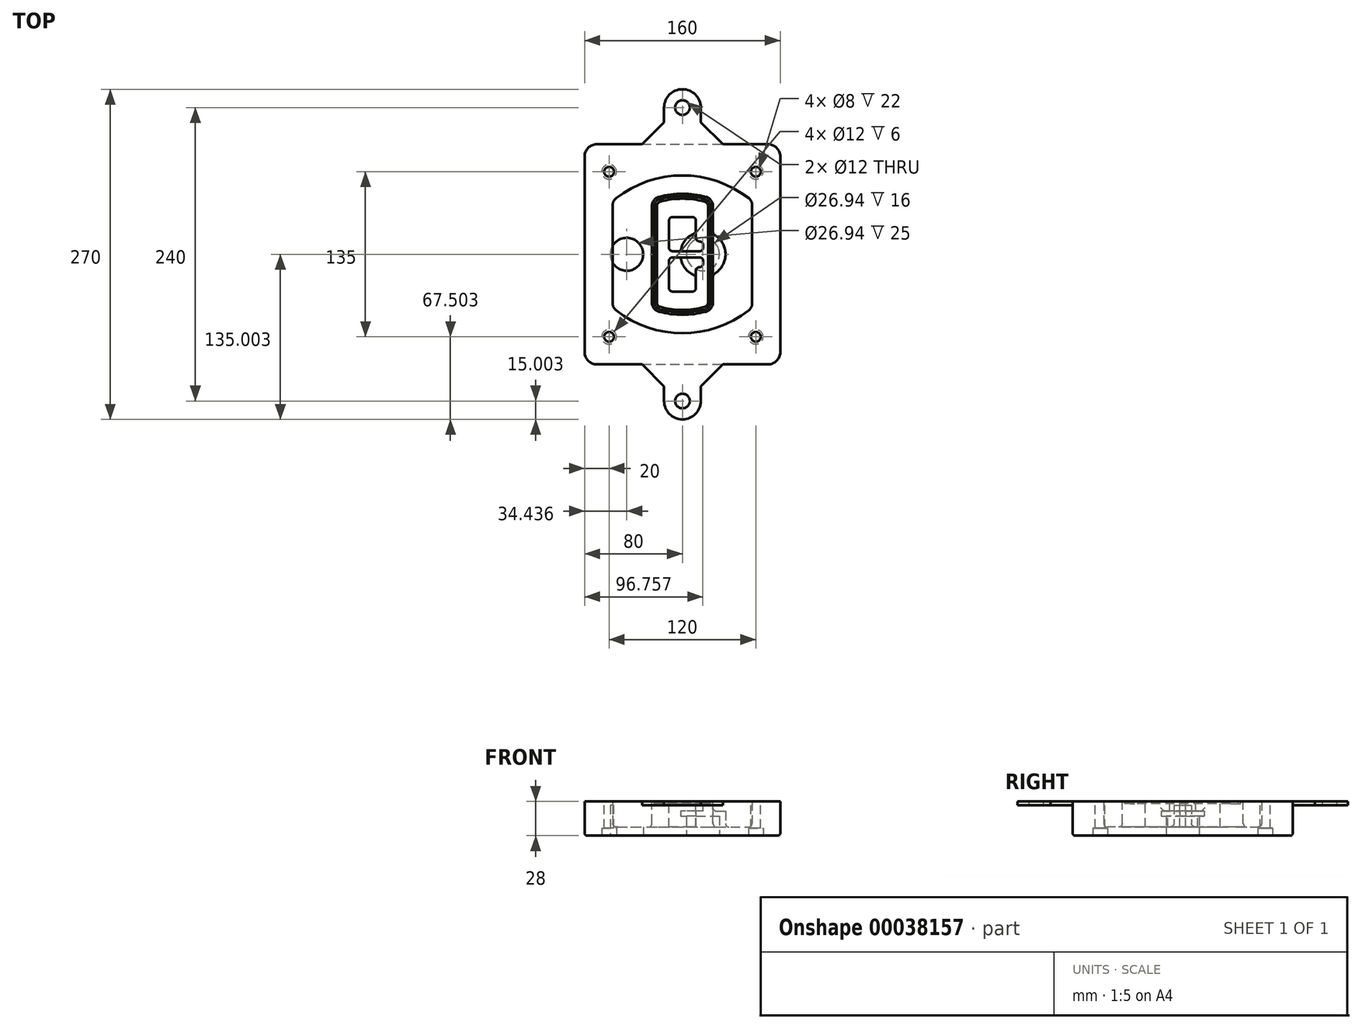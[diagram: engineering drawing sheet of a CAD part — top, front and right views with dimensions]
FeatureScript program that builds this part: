
annotation { "Feature Type Name" : "Feature", "Feature Type Description" : "" }
export const myFeature = defineFeature(function(context is Context, id is Id, definition is map)
    precondition{}
    {
        {
            var Q0;
            Q0=qCreatedBy(makeId("Top.planeOp"),FACE);
            var sketch = newSketch(context, id + "F0", { "sketchPlane" : qUnion([Q0])});
            skPoint(sketch, "E0.rect.middle", {"position": v(0, 0) * mm});
            skLineSegment(sketch, "E1.bottom", {"start": v(24.05, 28.38) * mm, "end": v(164.05, 28.38) * mm});
            skLineSegment(sketch, "E1.top", {"start": v(24.05, 208.38) * mm, "end": v(164.05, 208.38) * mm});
            skLineSegment(sketch, "E1.left", {"start": v(14.05, 38.38) * mm, "end": v(14.05, 198.38) * mm});
            skLineSegment(sketch, "E1.right", {"start": v(174.05, 38.38) * mm, "end": v(174.05, 198.38) * mm});
            skLineSegment(sketch, "E2", {"start": v(14.05, 208.38) * mm, "end": v(174.05, 28.38) * mm, "construction": true});
            skLineSegment(sketch, "E3", {"start": v(174.05, 208.38) * mm, "end": v(14.05, 28.38) * mm, "construction": true});
            skCircle(sketch, "E4", {"center": v(34.05, 185.88) * mm, "radius": 4 * mm});
            skCircle(sketch, "E5", {"center": v(154.05, 185.88) * mm, "radius": 4 * mm});
            skCircle(sketch, "E6", {"center": v(154.05, 50.88) * mm, "radius": 4 * mm});
            skCircle(sketch, "E7", {"center": v(34.05, 50.88) * mm, "radius": 4 * mm});
            skLineSegment(sketch, "E8", {"start": v(34.05, 185.88) * mm, "end": v(154.05, 185.88) * mm, "construction": true});
            skLineSegment(sketch, "E9", {"start": v(154.05, 185.88) * mm, "end": v(154.05, 50.88) * mm, "construction": true});
            skLineSegment(sketch, "E10", {"start": v(154.05, 50.88) * mm, "end": v(34.05, 50.88) * mm, "construction": true});
            skLineSegment(sketch, "E11", {"start": v(34.05, 50.88) * mm, "end": v(34.05, 185.88) * mm, "construction": true});
            skLineSegment(sketch, "E12", {"start": v(34.05, 158.68) * mm, "end": v(34.05, 78.09) * mm});
            skLineSegment(sketch, "E13", {"start": v(154.05, 158.68) * mm, "end": v(154.05, 78.09) * mm});
            skArc(sketch, "E14", {"start": v(150.2, 166.56) * mm, "mid": v(94.05, 185.88) * mm, "end": v(37.9, 166.56) * mm});
            skArc(sketch, "E15", {"start": v(37.9, 70.2) * mm, "mid": v(94.05, 50.88) * mm, "end": v(150.2, 70.2) * mm});
            skLineSegment(sketch, "E16", {"start": v(34.05, 118.38) * mm, "end": v(154.05, 118.38) * mm, "construction": true});
            skPoint(sketch, "E17.visualSharp", {"position": v(34.05, 73.38) * mm});
            skArc(sketch, "E17.filletArc", {"start": v(34.05, 78.09) * mm, "mid": v(35.06, 73.7) * mm, "end": v(37.9, 70.2) * mm});
            skPoint(sketch, "E18.visualSharp", {"position": v(34.05, 163.38) * mm});
            skArc(sketch, "E18.filletArc", {"start": v(37.9, 166.56) * mm, "mid": v(35.06, 163.06) * mm, "end": v(34.05, 158.68) * mm});
            skPoint(sketch, "E19.visualSharp", {"position": v(154.05, 163.38) * mm});
            skArc(sketch, "E19.filletArc", {"start": v(154.05, 158.68) * mm, "mid": v(153.04, 163.06) * mm, "end": v(150.2, 166.56) * mm});
            skPoint(sketch, "E20.visualSharp", {"position": v(154.05, 73.38) * mm});
            skArc(sketch, "E20.filletArc", {"start": v(150.2, 70.2) * mm, "mid": v(153.04, 73.7) * mm, "end": v(154.05, 78.09) * mm});
            skPoint(sketch, "E21.visualSharp", {"position": v(14.05, 208.38) * mm});
            skArc(sketch, "E21.filletArc", {"start": v(24.05, 208.38) * mm, "mid": v(16.98, 205.45) * mm, "end": v(14.05, 198.38) * mm});
            skPoint(sketch, "E22.visualSharp", {"position": v(174.05, 208.38) * mm});
            skArc(sketch, "E22.filletArc", {"start": v(174.05, 198.38) * mm, "mid": v(171.12, 205.45) * mm, "end": v(164.05, 208.38) * mm});
            skPoint(sketch, "E23.visualSharp", {"position": v(174.05, 28.38) * mm});
            skArc(sketch, "E23.filletArc", {"start": v(164.05, 28.38) * mm, "mid": v(171.12, 31.31) * mm, "end": v(174.05, 38.38) * mm});
            skPoint(sketch, "E24.visualSharp", {"position": v(14.05, 28.38) * mm});
            skArc(sketch, "E24.filletArc", {"start": v(14.05, 38.38) * mm, "mid": v(16.98, 31.31) * mm, "end": v(24.05, 28.38) * mm});
            skArc(sketch, "E25.0", {"start": v(151.05, 158.68) * mm, "mid": v(150.34, 161.75) * mm, "end": v(148.36, 164.2) * mm});
            skLineSegment(sketch, "E25.1", {"start": v(151.05, 158.68) * mm, "end": v(151.05, 78.09) * mm});
            skArc(sketch, "E25.2", {"start": v(148.36, 72.57) * mm, "mid": v(150.34, 75.02) * mm, "end": v(151.05, 78.09) * mm});
            skArc(sketch, "E25.3", {"start": v(39.74, 72.57) * mm, "mid": v(94.05, 53.88) * mm, "end": v(148.36, 72.57) * mm});
            skArc(sketch, "E25.4", {"start": v(37.05, 78.09) * mm, "mid": v(37.76, 75.02) * mm, "end": v(39.74, 72.57) * mm});
            skArc(sketch, "E25.5", {"start": v(148.36, 164.2) * mm, "mid": v(94.05, 182.88) * mm, "end": v(39.74, 164.2) * mm});
            skLineSegment(sketch, "E25.6", {"start": v(37.05, 158.68) * mm, "end": v(37.05, 78.09) * mm});
            skArc(sketch, "E25.7", {"start": v(39.74, 164.2) * mm, "mid": v(37.76, 161.75) * mm, "end": v(37.05, 158.68) * mm});
            skArc(sketch, "E26.0", {"start": v(35.43, 169.71) * mm, "mid": v(31.47, 164.82) * mm, "end": v(30.05, 158.68) * mm});
            skArc(sketch, "E26.1", {"start": v(152.67, 169.71) * mm, "mid": v(94.05, 189.88) * mm, "end": v(35.43, 169.71) * mm});
            skArc(sketch, "E26.2", {"start": v(158.05, 158.68) * mm, "mid": v(156.63, 164.82) * mm, "end": v(152.67, 169.71) * mm});
            skLineSegment(sketch, "E26.3", {"start": v(158.05, 158.68) * mm, "end": v(158.05, 78.09) * mm});
            skArc(sketch, "E26.4", {"start": v(152.67, 67.05) * mm, "mid": v(156.63, 71.95) * mm, "end": v(158.05, 78.09) * mm});
            skLineSegment(sketch, "E26.5", {"start": v(30.05, 158.68) * mm, "end": v(30.05, 78.09) * mm});
            skArc(sketch, "E26.6", {"start": v(35.43, 67.05) * mm, "mid": v(94.05, 46.88) * mm, "end": v(152.67, 67.05) * mm});
            skArc(sketch, "E26.7", {"start": v(30.05, 78.09) * mm, "mid": v(31.47, 71.95) * mm, "end": v(35.43, 67.05) * mm});
            skSolve(sketch);
        }
        {
            var Q0;
            Q0=makeQuery(id+"F0.imprint","IMPRINT",FACE,{"disambiguationData":[TD([[makeQuery(id+"F0.imprint","IMPRINT",EDGE,{"derivedFrom":sQuery(id+"F0.wireOp",EDGE,"E1.bottom")}),1.0]])]});
            var Q1;
            Q1=makeQuery(id+"F0.imprint","IMPRINT",FACE,{"disambiguationData":[TD([[makeQuery(id+"F0.imprint","IMPRINT",EDGE,{"derivedFrom":sQuery(id+"F0.wireOp",EDGE,"E12")}),1.0]])]});
            var Q2;
            Q2=makeQuery(id+"F0.imprint","IMPRINT",FACE,{"disambiguationData":[TD([[makeQuery(id+"F0.imprint","IMPRINT",EDGE,{"derivedFrom":sQuery(id+"F0.wireOp",EDGE,"E25.0")}),1.0]])]});
            var Q3;
            Q3=makeQuery(id+"F0.imprint","IMPRINT",FACE,{"disambiguationData":[TD([[makeQuery(id+"F0.imprint","IMPRINT",EDGE,{"derivedFrom":sQuery(id+"F0.wireOp",EDGE,"E12")}),-1.0]])]});
            extrude(context, id + "F1", {"entities" : qUnion([Q0, Q1, Q2, Q3]), "oppositeDirection" : true, "depth" : 25 * mm});
        }
        {
            var Q0;
            Q0=makeQuery(id+"F0.imprint","IMPRINT",FACE,{"disambiguationData":[TD([[makeQuery(id+"F0.imprint","IMPRINT",EDGE,{"derivedFrom":sQuery(id+"F0.wireOp",EDGE,"E12")}),1.0]])]});
            extrude(context, id + "F2", {"entities" : qUnion([Q0]), "operationType" : NewBodyOperationType.ADD, "depth" : 3 * mm});
        }
        {
            var Q0;
            Q0=makeQuery(id+"F0.imprint","IMPRINT",FACE,{"disambiguationData":[TD([[makeQuery(id+"F0.imprint","IMPRINT",EDGE,{"derivedFrom":sQuery(id+"F0.wireOp",EDGE,"E25.0")}),1.0]])]});
            extrude(context, id + "F3", {"entities" : qUnion([Q0]), "operationType" : NewBodyOperationType.REMOVE, "oppositeDirection" : true, "depth" : 18 * mm});
        }
        {
            var Q0;
            Q0=makeQuery(id+"F2.opExtrude","CAP_FACE",FACE,{"disambiguationData":[OSD([sQuery(id+"F0.wireOp",EDGE,"E12"),sQuery(id+"F0.wireOp",EDGE,"E13"),sQuery(id+"F0.wireOp",EDGE,"E14"),sQuery(id+"F0.wireOp",EDGE,"E15"),sQuery(id+"F0.wireOp",EDGE,"E17.filletArc"),sQuery(id+"F0.wireOp",EDGE,"E18.filletArc"),sQuery(id+"F0.wireOp",EDGE,"E19.filletArc"),sQuery(id+"F0.wireOp",EDGE,"E20.filletArc"),sQuery(id+"F0.wireOp",EDGE,"E25.0"),sQuery(id+"F0.wireOp",EDGE,"E25.1"),sQuery(id+"F0.wireOp",EDGE,"E25.2"),sQuery(id+"F0.wireOp",EDGE,"E25.3"),sQuery(id+"F0.wireOp",EDGE,"E25.4"),sQuery(id+"F0.wireOp",EDGE,"E25.5"),sQuery(id+"F0.wireOp",EDGE,"E25.6"),sQuery(id+"F0.wireOp",EDGE,"E25.7")])],"isStart":false});
            var sketch = newSketch(context, id + "F4", { "sketchPlane" : qUnion([Q0])});
            skArc(sketch, "E27.0", {"start": v(74.97, 71.41) * mm, "mid": v(94.05, 68.88) * mm, "end": v(113.13, 71.41) * mm});
            skArc(sketch, "E28.0", {"start": v(113.13, 165.35) * mm, "mid": v(94.05, 167.88) * mm, "end": v(74.97, 165.35) * mm});
            skLineSegment(sketch, "E29", {"start": v(69.05, 157.63) * mm, "end": v(69.05, 79.14) * mm});
            skLineSegment(sketch, "E30", {"start": v(119.05, 157.63) * mm, "end": v(119.05, 79.14) * mm});
            skLineSegment(sketch, "E31", {"start": v(69.05, 163.48) * mm, "end": v(119.05, 163.48) * mm, "construction": true});
            skLineSegment(sketch, "E32", {"start": v(69.05, 73.28) * mm, "end": v(119.05, 73.28) * mm, "construction": true});
            skPoint(sketch, "E33.visualSharp", {"position": v(69.05, 163.48) * mm});
            skArc(sketch, "E33.filletArc", {"start": v(74.97, 165.35) * mm, "mid": v(70.7, 162.5) * mm, "end": v(69.05, 157.63) * mm});
            skPoint(sketch, "E34.visualSharp", {"position": v(119.05, 163.48) * mm});
            skArc(sketch, "E34.filletArc", {"start": v(119.05, 157.63) * mm, "mid": v(117.4, 162.5) * mm, "end": v(113.13, 165.35) * mm});
            skPoint(sketch, "E35.visualSharp", {"position": v(119.05, 73.28) * mm});
            skArc(sketch, "E35.filletArc", {"start": v(113.13, 71.41) * mm, "mid": v(117.4, 74.27) * mm, "end": v(119.05, 79.14) * mm});
            skPoint(sketch, "E36.visualSharp", {"position": v(69.05, 73.28) * mm});
            skArc(sketch, "E36.filletArc", {"start": v(69.05, 79.14) * mm, "mid": v(70.7, 74.27) * mm, "end": v(74.97, 71.41) * mm});
            skArc(sketch, "E37.0", {"start": v(148.36, 164.2) * mm, "mid": v(94.05, 182.88) * mm, "end": v(39.74, 164.2) * mm});
            skArc(sketch, "E37.1", {"start": v(39.74, 164.2) * mm, "mid": v(37.76, 161.75) * mm, "end": v(37.05, 158.68) * mm});
            skLineSegment(sketch, "E37.2", {"start": v(37.05, 158.68) * mm, "end": v(37.05, 78.09) * mm});
            skArc(sketch, "E37.3", {"start": v(37.05, 78.09) * mm, "mid": v(37.76, 75.02) * mm, "end": v(39.74, 72.57) * mm});
            skArc(sketch, "E37.4", {"start": v(39.74, 72.57) * mm, "mid": v(94.05, 53.88) * mm, "end": v(148.36, 72.57) * mm});
            skArc(sketch, "E37.5", {"start": v(148.36, 72.57) * mm, "mid": v(150.34, 75.02) * mm, "end": v(151.05, 78.09) * mm});
            skLineSegment(sketch, "E37.6", {"start": v(151.05, 158.68) * mm, "end": v(151.05, 78.09) * mm});
            skArc(sketch, "E37.7", {"start": v(151.05, 158.68) * mm, "mid": v(150.34, 161.75) * mm, "end": v(148.36, 164.2) * mm});
            skLineSegment(sketch, "E38.0", {"start": v(117.05, 157.63) * mm, "end": v(117.05, 79.14) * mm});
            skArc(sketch, "E38.1", {"start": v(112.61, 73.34) * mm, "mid": v(115.81, 75.49) * mm, "end": v(117.05, 79.14) * mm});
            skArc(sketch, "E38.2", {"start": v(75.49, 73.34) * mm, "mid": v(94.05, 70.88) * mm, "end": v(112.61, 73.34) * mm});
            skArc(sketch, "E38.3", {"start": v(71.05, 79.14) * mm, "mid": v(72.29, 75.49) * mm, "end": v(75.49, 73.34) * mm});
            skLineSegment(sketch, "E38.4", {"start": v(71.05, 157.63) * mm, "end": v(71.05, 79.14) * mm});
            skArc(sketch, "E38.5", {"start": v(117.05, 157.63) * mm, "mid": v(115.81, 161.28) * mm, "end": v(112.61, 163.42) * mm});
            skArc(sketch, "E38.6", {"start": v(75.49, 163.42) * mm, "mid": v(72.29, 161.28) * mm, "end": v(71.05, 157.63) * mm});
            skArc(sketch, "E38.7", {"start": v(112.61, 163.42) * mm, "mid": v(94.05, 165.88) * mm, "end": v(75.49, 163.42) * mm});
            skArc(sketch, "E39.0", {"start": v(115.05, 157.63) * mm, "mid": v(114.23, 160.06) * mm, "end": v(112.1, 161.5) * mm});
            skLineSegment(sketch, "E39.1", {"start": v(115.05, 157.63) * mm, "end": v(115.05, 79.14) * mm});
            skArc(sketch, "E39.2", {"start": v(112.1, 75.27) * mm, "mid": v(114.23, 76.7) * mm, "end": v(115.05, 79.14) * mm});
            skArc(sketch, "E39.3", {"start": v(76, 75.27) * mm, "mid": v(94.05, 72.88) * mm, "end": v(112.1, 75.27) * mm});
            skArc(sketch, "E39.4", {"start": v(73.05, 79.14) * mm, "mid": v(73.87, 76.7) * mm, "end": v(76, 75.27) * mm});
            skArc(sketch, "E39.5", {"start": v(112.1, 161.5) * mm, "mid": v(94.05, 163.88) * mm, "end": v(76, 161.5) * mm});
            skLineSegment(sketch, "E39.6", {"start": v(73.05, 157.63) * mm, "end": v(73.05, 79.14) * mm});
            skArc(sketch, "E39.7", {"start": v(76, 161.5) * mm, "mid": v(73.87, 160.06) * mm, "end": v(73.05, 157.63) * mm});
            skLineSegment(sketch, "E40", {"start": v(69.05, 118.38) * mm, "end": v(119.05, 118.38) * mm, "construction": true});
            skLineSegment(sketch, "E41", {"start": v(83.05, 123.88) * mm, "end": v(83.05, 145.88) * mm});
            skLineSegment(sketch, "E42", {"start": v(86.05, 148.88) * mm, "end": v(102.05, 148.88) * mm});
            skLineSegment(sketch, "E43", {"start": v(105.05, 145.88) * mm, "end": v(105.05, 131.88) * mm});
            skLineSegment(sketch, "E44", {"start": v(108.05, 128.88) * mm, "end": v(108.05, 128.88) * mm});
            skLineSegment(sketch, "E45", {"start": v(111.05, 125.88) * mm, "end": v(111.05, 123.88) * mm});
            skLineSegment(sketch, "E46", {"start": v(108.05, 120.88) * mm, "end": v(86.05, 120.88) * mm});
            skPoint(sketch, "E47.visualSharp", {"position": v(83.05, 148.88) * mm});
            skArc(sketch, "E47.filletArc", {"start": v(86.05, 148.88) * mm, "mid": v(83.93, 148) * mm, "end": v(83.05, 145.88) * mm});
            skPoint(sketch, "E48.visualSharp", {"position": v(105.05, 148.88) * mm});
            skArc(sketch, "E48.filletArc", {"start": v(105.05, 145.88) * mm, "mid": v(104.17, 148) * mm, "end": v(102.05, 148.88) * mm});
            skPoint(sketch, "E49.visualSharp", {"position": v(105.05, 128.88) * mm});
            skArc(sketch, "E49.filletArc", {"start": v(105.05, 131.88) * mm, "mid": v(105.93, 129.76) * mm, "end": v(108.05, 128.88) * mm});
            skPoint(sketch, "E50.visualSharp", {"position": v(111.05, 128.88) * mm});
            skArc(sketch, "E50.filletArc", {"start": v(111.05, 125.88) * mm, "mid": v(110.17, 128) * mm, "end": v(108.05, 128.88) * mm});
            skPoint(sketch, "E51.visualSharp", {"position": v(111.05, 120.88) * mm});
            skArc(sketch, "E51.filletArc", {"start": v(108.05, 120.88) * mm, "mid": v(110.17, 121.76) * mm, "end": v(111.05, 123.88) * mm});
            skPoint(sketch, "E52.visualSharp", {"position": v(83.05, 120.88) * mm});
            skArc(sketch, "E52.filletArc", {"start": v(83.05, 123.88) * mm, "mid": v(83.93, 121.76) * mm, "end": v(86.05, 120.88) * mm});
            skLineSegment(sketch, "E53.0.MirrorCS", {"start": v(108.05, 115.88) * mm, "end": v(86.05, 115.88) * mm});
            skArc(sketch, "E54.0.MirrorCS", {"start": v(83.05, 112.88) * mm, "mid": v(83.93, 115) * mm, "end": v(86.05, 115.88) * mm});
            skLineSegment(sketch, "E55.0.MirrorCS", {"start": v(83.05, 112.88) * mm, "end": v(83.05, 90.88) * mm});
            skArc(sketch, "E56.0.MirrorCS", {"start": v(86.05, 87.88) * mm, "mid": v(83.93, 88.76) * mm, "end": v(83.05, 90.88) * mm});
            skLineSegment(sketch, "E57.0.MirrorCS", {"start": v(86.05, 87.88) * mm, "end": v(102.05, 87.88) * mm});
            skArc(sketch, "E58.0.MirrorCS", {"start": v(105.05, 90.88) * mm, "mid": v(104.17, 88.76) * mm, "end": v(102.05, 87.88) * mm});
            skLineSegment(sketch, "E59.0.MirrorCS", {"start": v(105.05, 90.88) * mm, "end": v(105.05, 104.88) * mm});
            skArc(sketch, "E60.0.MirrorCS", {"start": v(105.05, 104.88) * mm, "mid": v(105.93, 107) * mm, "end": v(108.05, 107.88) * mm});
            skArc(sketch, "E61.0.MirrorCS", {"start": v(111.05, 110.88) * mm, "mid": v(110.17, 108.76) * mm, "end": v(108.05, 107.88) * mm});
            skLineSegment(sketch, "E62.0.MirrorCS", {"start": v(111.05, 110.88) * mm, "end": v(111.05, 112.88) * mm});
            skArc(sketch, "E63.0.MirrorCS", {"start": v(108.05, 115.88) * mm, "mid": v(110.17, 115) * mm, "end": v(111.05, 112.88) * mm});
            skSolve(sketch);
        }
        {
            var Q0;
            Q0=makeQuery(id+"F4.imprint","IMPRINT",FACE,{"disambiguationData":[TD([[makeQuery(id+"F4.imprint","IMPRINT",EDGE,{"derivedFrom":sQuery(id+"F4.wireOp",EDGE,"E27.0")}),1.0]])]});
            var Q1;
            Q1=makeQuery(id+"F4.imprint","IMPRINT",FACE,{"disambiguationData":[TD([[makeQuery(id+"F4.imprint","IMPRINT",EDGE,{"derivedFrom":sQuery(id+"F4.wireOp",EDGE,"E38.0")}),-1.0]])]});
            var Q2;
            Q2=makeQuery(id+"F4.imprint","IMPRINT",FACE,{"disambiguationData":[TD([[makeQuery(id+"F4.imprint","IMPRINT",EDGE,{"derivedFrom":sQuery(id+"F4.wireOp",EDGE,"E39.0")}),1.0]])]});
            extrude(context, id + "F5", {"entities" : qUnion([Q0, Q1, Q2]), "operationType" : NewBodyOperationType.ADD, "endBound" : BoundingType.UP_TO_NEXT, "oppositeDirection" : true, "depth" : 25 * mm});
        }
        {
            var Q0;
            Q0=makeQuery(id+"F4.imprint","IMPRINT",FACE,{"disambiguationData":[TD([[makeQuery(id+"F4.imprint","IMPRINT",EDGE,{"derivedFrom":sQuery(id+"F4.wireOp",EDGE,"E38.0")}),-1.0]])]});
            extrude(context, id + "F6", {"entities" : qUnion([Q0]), "operationType" : NewBodyOperationType.REMOVE, "oppositeDirection" : true, "depth" : 2 * mm});
        }
        {
            var Q0;
            Q0=makeQuery(id+"F1.opExtrude","CAP_FACE",FACE,{"disambiguationData":[OSD([sQuery(id+"F0.wireOp",EDGE,"E1.bottom"),sQuery(id+"F0.wireOp",EDGE,"E1.top"),sQuery(id+"F0.wireOp",EDGE,"E1.left"),sQuery(id+"F0.wireOp",EDGE,"E1.right"),sQuery(id+"F0.wireOp",EDGE,"E4"),sQuery(id+"F0.wireOp",EDGE,"E5"),sQuery(id+"F0.wireOp",EDGE,"E6"),sQuery(id+"F0.wireOp",EDGE,"E7"),sQuery(id+"F0.wireOp",EDGE,"E21.filletArc"),sQuery(id+"F0.wireOp",EDGE,"E22.filletArc"),sQuery(id+"F0.wireOp",EDGE,"E23.filletArc"),sQuery(id+"F0.wireOp",EDGE,"E24.filletArc")])],"isStart":false});
            var sketch = newSketch(context, id + "F7", { "sketchPlane" : qUnion([Q0])});
            skCircle(sketch, "E64", {"center": v(110.8, -118.38) * mm, "radius": 13.47 * mm});
            skCircle(sketch, "E65", {"center": v(48.49, -118.38) * mm, "radius": 13.47 * mm});
            skLineSegment(sketch, "E66", {"start": v(174.05, -118.38) * mm, "end": v(14.05, -118.38) * mm});
            skCircle(sketch, "E67", {"center": v(110.8, -118.38) * mm, "radius": 18.47 * mm});
            skCircle(sketch, "E68", {"center": v(154.05, -185.88) * mm, "radius": 6 * mm});
            skCircle(sketch, "E69", {"center": v(34.05, -185.88) * mm, "radius": 6 * mm});
            skCircle(sketch, "E70", {"center": v(34.05, -50.88) * mm, "radius": 6 * mm});
            skCircle(sketch, "E71", {"center": v(154.05, -50.88) * mm, "radius": 6 * mm});
            skSolve(sketch);
        }
        {
            var Q0;
            {var subQ1=sQuery(id+"F7.wireOp",EDGE,"E66");var subQ4=sQuery(id+"F7.wireOp",EDGE,"E64");var subQ6=makeQuery(id+"F7.imprint","INTERSECT",VERTEX,{"disambiguationData":[OD(0.0)],"derivedFrom":[subQ4,subQ1]});Q0=makeQuery(id+"F7.imprint","IMPRINT",FACE,{"disambiguationData":[TD([[makeQuery(id+"F7.imprint","IMPRINT",EDGE,{"disambiguationData":[TD([[subQ6,-1.0]])],"derivedFrom":subQ4}),-1.0]])]});}
            var Q1;
            {var subQ0=sQuery(id+"F7.wireOp",EDGE,"E66");var subQ1=sQuery(id+"F7.wireOp",EDGE,"E64");var subQ3=makeQuery(id+"F7.imprint","INTERSECT",VERTEX,{"disambiguationData":[OD(0.0)],"derivedFrom":[subQ1,subQ0]});Q1=makeQuery(id+"F7.imprint","IMPRINT",FACE,{"disambiguationData":[TD([[makeQuery(id+"F7.imprint","IMPRINT",EDGE,{"disambiguationData":[TD([[subQ3,-1.0]])],"derivedFrom":subQ1}),1.0]])]});}
            var Q2;
            {var subQ0=sQuery(id+"F7.wireOp",EDGE,"E66");var subQ1=sQuery(id+"F7.wireOp",EDGE,"E64");var subQ3=makeQuery(id+"F7.imprint","INTERSECT",VERTEX,{"disambiguationData":[OD(0.0)],"derivedFrom":[subQ1,subQ0]});Q2=makeQuery(id+"F7.imprint","IMPRINT",FACE,{"disambiguationData":[TD([[makeQuery(id+"F7.imprint","IMPRINT",EDGE,{"disambiguationData":[TD([[subQ3,1.0]])],"derivedFrom":subQ1}),1.0]])]});}
            var Q3;
            {var subQ1=sQuery(id+"F7.wireOp",EDGE,"E66");var subQ4=sQuery(id+"F7.wireOp",EDGE,"E64");var subQ6=makeQuery(id+"F7.imprint","INTERSECT",VERTEX,{"disambiguationData":[OD(0.0)],"derivedFrom":[subQ4,subQ1]});Q3=makeQuery(id+"F7.imprint","IMPRINT",FACE,{"disambiguationData":[TD([[makeQuery(id+"F7.imprint","IMPRINT",EDGE,{"disambiguationData":[TD([[subQ6,1.0]])],"derivedFrom":subQ4}),-1.0]])]});}
            extrude(context, id + "F8", {"entities" : qUnion([Q0, Q1, Q2, Q3]), "operationType" : NewBodyOperationType.ADD, "oppositeDirection" : true, "depth" : 20 * mm});
        }
        {
            var Q0;
            {var subQ0=sQuery(id+"F7.wireOp",EDGE,"E66");var subQ1=sQuery(id+"F7.wireOp",EDGE,"E64");var subQ3=makeQuery(id+"F7.imprint","INTERSECT",VERTEX,{"disambiguationData":[OD(0.0)],"derivedFrom":[subQ1,subQ0]});Q0=makeQuery(id+"F7.imprint","IMPRINT",FACE,{"disambiguationData":[TD([[makeQuery(id+"F7.imprint","IMPRINT",EDGE,{"disambiguationData":[TD([[subQ3,-1.0]])],"derivedFrom":subQ1}),1.0]])]});}
            var Q1;
            {var subQ0=sQuery(id+"F7.wireOp",EDGE,"E66");var subQ1=sQuery(id+"F7.wireOp",EDGE,"E64");var subQ3=makeQuery(id+"F7.imprint","INTERSECT",VERTEX,{"disambiguationData":[OD(0.0)],"derivedFrom":[subQ1,subQ0]});Q1=makeQuery(id+"F7.imprint","IMPRINT",FACE,{"disambiguationData":[TD([[makeQuery(id+"F7.imprint","IMPRINT",EDGE,{"disambiguationData":[TD([[subQ3,1.0]])],"derivedFrom":subQ1}),1.0]])]});}
            extrude(context, id + "F9", {"entities" : qUnion([Q0, Q1]), "operationType" : NewBodyOperationType.REMOVE, "oppositeDirection" : true, "depth" : 16 * mm});
        }
        {
            var Q0;
            {var subQ0=sQuery(id+"F7.wireOp",EDGE,"E66");var subQ1=sQuery(id+"F7.wireOp",EDGE,"E65");var subQ3=makeQuery(id+"F7.imprint","INTERSECT",VERTEX,{"disambiguationData":[OD(0.0)],"derivedFrom":[subQ1,subQ0]});Q0=makeQuery(id+"F7.imprint","IMPRINT",FACE,{"disambiguationData":[TD([[makeQuery(id+"F7.imprint","IMPRINT",EDGE,{"disambiguationData":[TD([[subQ3,-1.0]])],"derivedFrom":subQ1}),1.0]])]});}
            var Q1;
            {var subQ0=sQuery(id+"F7.wireOp",EDGE,"E66");var subQ1=sQuery(id+"F7.wireOp",EDGE,"E65");var subQ3=makeQuery(id+"F7.imprint","INTERSECT",VERTEX,{"disambiguationData":[OD(0.0)],"derivedFrom":[subQ1,subQ0]});Q1=makeQuery(id+"F7.imprint","IMPRINT",FACE,{"disambiguationData":[TD([[makeQuery(id+"F7.imprint","IMPRINT",EDGE,{"disambiguationData":[TD([[subQ3,1.0]])],"derivedFrom":subQ1}),1.0]])]});}
            extrude(context, id + "F10", {"entities" : qUnion([Q0, Q1]), "operationType" : NewBodyOperationType.REMOVE, "oppositeDirection" : true, "depth" : 25 * mm});
        }
        {
            var Q0;
            Q0=makeQuery(id+"F7.imprint","IMPRINT",FACE,{"disambiguationData":[TD([[makeQuery(id+"F7.imprint","IMPRINT",EDGE,{"derivedFrom":sQuery(id+"F7.wireOp",EDGE,"E68")}),1.0]])]});
            var Q1;
            Q1=makeQuery(id+"F7.imprint","IMPRINT",FACE,{"disambiguationData":[TD([[makeQuery(id+"F7.imprint","IMPRINT",EDGE,{"derivedFrom":makeQuery(id+"F1.opExtrude","CAP_EDGE",EDGE,{"disambiguationData":[OSD([sQuery(id+"F0.wireOp",EDGE,"E5")])],"isStart":false})}),-1.0]])]});
            var Q2;
            Q2=makeQuery(id+"F7.imprint","IMPRINT",FACE,{"disambiguationData":[TD([[makeQuery(id+"F7.imprint","IMPRINT",EDGE,{"derivedFrom":sQuery(id+"F7.wireOp",EDGE,"E69")}),1.0]])]});
            var Q3;
            Q3=makeQuery(id+"F7.imprint","IMPRINT",FACE,{"disambiguationData":[TD([[makeQuery(id+"F7.imprint","IMPRINT",EDGE,{"derivedFrom":makeQuery(id+"F1.opExtrude","CAP_EDGE",EDGE,{"disambiguationData":[OSD([sQuery(id+"F0.wireOp",EDGE,"E4")])],"isStart":false})}),-1.0]])]});
            var Q4;
            Q4=makeQuery(id+"F7.imprint","IMPRINT",FACE,{"disambiguationData":[TD([[makeQuery(id+"F7.imprint","IMPRINT",EDGE,{"derivedFrom":sQuery(id+"F7.wireOp",EDGE,"E70")}),1.0]])]});
            var Q5;
            Q5=makeQuery(id+"F7.imprint","IMPRINT",FACE,{"disambiguationData":[TD([[makeQuery(id+"F7.imprint","IMPRINT",EDGE,{"derivedFrom":makeQuery(id+"F1.opExtrude","CAP_EDGE",EDGE,{"disambiguationData":[OSD([sQuery(id+"F0.wireOp",EDGE,"E7")])],"isStart":false})}),-1.0]])]});
            var Q6;
            Q6=makeQuery(id+"F7.imprint","IMPRINT",FACE,{"disambiguationData":[TD([[makeQuery(id+"F7.imprint","IMPRINT",EDGE,{"derivedFrom":sQuery(id+"F7.wireOp",EDGE,"E71")}),1.0]])]});
            var Q7;
            Q7=makeQuery(id+"F7.imprint","IMPRINT",FACE,{"disambiguationData":[TD([[makeQuery(id+"F7.imprint","IMPRINT",EDGE,{"derivedFrom":makeQuery(id+"F1.opExtrude","CAP_EDGE",EDGE,{"disambiguationData":[OSD([sQuery(id+"F0.wireOp",EDGE,"E6")])],"isStart":false})}),-1.0]])]});
            extrude(context, id + "F11", {"entities" : qUnion([Q0, Q1, Q2, Q3, Q4, Q5, Q6, Q7]), "operationType" : NewBodyOperationType.REMOVE, "oppositeDirection" : true, "depth" : 6 * mm});
        }
        {
            var Q0;
            Q0=makeQuery(id+"F9.boolean.opBoolean","COPY",FACE,{"derivedFrom":makeQuery(id+"F9.opExtrude","CAP_FACE",FACE,{"disambiguationData":[OSD([sQuery(id+"F7.wireOp",EDGE,"E64")])],"isStart":false})});
            var sketch = newSketch(context, id + "F12", { "sketchPlane" : qUnion([Q0])});
            skArc(sketch, "E72.0", {"start": v(105.05, -100.83) * mm, "mid": v(96.62, -106.56) * mm, "end": v(92.5, -115.88) * mm});
            skArc(sketch, "E72.1", {"start": v(92.5, -120.88) * mm, "mid": v(96.62, -130.2) * mm, "end": v(105.05, -135.93) * mm});
            skLineSegment(sketch, "E73", {"start": v(92.5, -120.88) * mm, "end": v(108.05, -120.88) * mm});
            skLineSegment(sketch, "E74.0", {"start": v(108.05, -115.88) * mm, "end": v(92.5, -115.88) * mm});
            skArc(sketch, "E74.1", {"start": v(108.05, -115.88) * mm, "mid": v(110.17, -115) * mm, "end": v(111.05, -112.88) * mm});
            skLineSegment(sketch, "E74.2", {"start": v(111.05, -110.88) * mm, "end": v(111.05, -112.88) * mm});
            skArc(sketch, "E74.3", {"start": v(111.05, -110.88) * mm, "mid": v(110.17, -108.76) * mm, "end": v(108.05, -107.88) * mm});
            skArc(sketch, "E74.4", {"start": v(105.05, -104.88) * mm, "mid": v(105.93, -107) * mm, "end": v(108.05, -107.88) * mm});
            skLineSegment(sketch, "E74.5", {"start": v(105.05, -100.83) * mm, "end": v(105.05, -104.88) * mm});
            skLineSegment(sketch, "E74.7", {"start": v(108.05, -120.88) * mm, "end": v(92.5, -120.88) * mm});
            skArc(sketch, "E74.8", {"start": v(108.05, -120.88) * mm, "mid": v(110.17, -121.76) * mm, "end": v(111.05, -123.88) * mm});
            skLineSegment(sketch, "E74.9", {"start": v(111.05, -125.88) * mm, "end": v(111.05, -123.88) * mm});
            skArc(sketch, "E74.10", {"start": v(111.05, -125.88) * mm, "mid": v(110.17, -128) * mm, "end": v(108.05, -128.88) * mm});
            skArc(sketch, "E74.11", {"start": v(105.05, -131.88) * mm, "mid": v(105.93, -129.76) * mm, "end": v(108.05, -128.88) * mm});
            skLineSegment(sketch, "E74.12", {"start": v(105.05, -135.93) * mm, "end": v(105.05, -131.88) * mm});
            skPoint(sketch, "E75.orphan", {"position": v(105.05, -145.88) * mm});
            skPoint(sketch, "E76.orphan", {"position": v(86.05, -120.88) * mm});
            skPoint(sketch, "E77.orphan", {"position": v(86.05, -115.88) * mm});
            skPoint(sketch, "E78.orphan", {"position": v(105.05, -90.88) * mm});
            skSolve(sketch);
        }
        {
            var Q0;
            {var subQ7=sQuery(id+"F12.wireOp",EDGE,"E72.0");var subQ14=sQuery(id+"F12.wireOp",EDGE,"E72.1");var subQ16=sQuery(id+"F12.wireOp",EDGE,"E74.1");var subQ18=sQuery(id+"F12.wireOp",EDGE,"E74.8");Q0=qUnion([makeQuery(id+"F12.imprint","IMPRINT",FACE,{"disambiguationData":[TD([[makeQuery(id+"F12.imprint","IMPRINT",EDGE,{"derivedFrom":subQ7}),1.0]])]}),makeQuery(id+"F12.imprint","IMPRINT",FACE,{"disambiguationData":[TD([[makeQuery(id+"F12.imprint","IMPRINT",EDGE,{"derivedFrom":subQ14}),1.0]])]}),makeQuery(id+"F12.imprint","IMPRINT",FACE,{"disambiguationData":[TD([[makeQuery(id+"F12.imprint","IMPRINT",EDGE,{"derivedFrom":subQ16}),1.0]])]}),makeQuery(id+"F12.imprint","IMPRINT",FACE,{"disambiguationData":[TD([[makeQuery(id+"F12.imprint","IMPRINT",EDGE,{"derivedFrom":subQ18}),-1.0]])]})]);}
            var Q1;
            Q1=makeQuery(id+"F5.boolean.opBoolean","SPLIT",FACE,{"disambiguationData":[TD([makeQuery(id+"F5.opExtrude","SWEPT_FACE",FACE,{"disambiguationData":[OSD([sQuery(id+"F4.wireOp",EDGE,"E41")])]})])],"derivedFrom":makeQuery(id+"F3.boolean.opBoolean","COPY",FACE,{"derivedFrom":makeQuery(id+"F3.opExtrude","CAP_FACE",FACE,{"disambiguationData":[OSD([sQuery(id+"F0.wireOp",EDGE,"E25.0"),sQuery(id+"F0.wireOp",EDGE,"E25.1"),sQuery(id+"F0.wireOp",EDGE,"E25.2"),sQuery(id+"F0.wireOp",EDGE,"E25.3"),sQuery(id+"F0.wireOp",EDGE,"E25.4"),sQuery(id+"F0.wireOp",EDGE,"E25.5"),sQuery(id+"F0.wireOp",EDGE,"E25.6"),sQuery(id+"F0.wireOp",EDGE,"E25.7")])],"isStart":false})})});
            extrude(context, id + "F13", {"entities" : qUnion([Q0]), "operationType" : NewBodyOperationType.REMOVE, "endBound" : BoundingType.UP_TO_SURFACE, "endBoundEntityFace" : qUnion([Q1]), "depth" : 25 * mm});
        }
        {
            var Q0;
            Q0=makeQuery(id+"F3.boolean.opBoolean","COPY",EDGE,{"derivedFrom":makeQuery(id+"F3.opExtrude","CAP_EDGE",EDGE,{"disambiguationData":[OSD([sQuery(id+"F0.wireOp",EDGE,"E25.6")])],"isStart":false})});
            var Q1;
            Q1=makeQuery(id+"F8.boolean.opBoolean","INTERSECT",EDGE,{"derivedFrom":[makeQuery(id+"F5.opExtrude","SWEPT_FACE",FACE,{"disambiguationData":[OSD([sQuery(id+"F4.wireOp",EDGE,"E30")])]}),makeQuery(id+"F8.opExtrude","CAP_FACE",FACE,{"disambiguationData":[OSD([sQuery(id+"F7.wireOp",EDGE,"E67")])],"isStart":false})]});
            var Q2;
            Q2=makeQuery(id+"F8.boolean.opBoolean","INTERSECT",EDGE,{"disambiguationData":[OD(1.0)],"derivedFrom":[makeQuery(id+"F5.opExtrude","SWEPT_FACE",FACE,{"disambiguationData":[OSD([sQuery(id+"F4.wireOp",EDGE,"E30")])]}),makeQuery(id+"F8.opExtrude","SWEPT_FACE",FACE,{"disambiguationData":[OSD([sQuery(id+"F7.wireOp",EDGE,"E67")])]})]});
            var Q3;
            {var subQ0=sQuery(id+"F4.wireOp",EDGE,"E30");Q3=makeQuery(id+"F8.boolean.opBoolean","SPLIT",EDGE,{"disambiguationData":[TD([makeQuery(id+"F5.opExtrude","SWEPT_FACE",FACE,{"disambiguationData":[OSD([sQuery(id+"F4.wireOp",EDGE,"E35.filletArc")])]})])],"derivedFrom":makeQuery(id+"F5.opExtrude","CAP_EDGE",EDGE,{"disambiguationData":[OSD([subQ0])],"isStart":false})});}
            var Q4;
            {var subQ0=sQuery(id+"F0.wireOp",EDGE,"E25.7");var subQ1=sQuery(id+"F0.wireOp",EDGE,"E25.1");var subQ2=sQuery(id+"F0.wireOp",EDGE,"E25.6");var subQ3=sQuery(id+"F0.wireOp",EDGE,"E25.5");var subQ4=sQuery(id+"F0.wireOp",EDGE,"E25.4");var subQ5=sQuery(id+"F0.wireOp",EDGE,"E25.0");var subQ6=sQuery(id+"F0.wireOp",EDGE,"E25.2");var subQ7=sQuery(id+"F0.wireOp",EDGE,"E25.3");Q4=makeQuery(id+"F8.boolean.opBoolean","INTERSECT",EDGE,{"derivedFrom":[makeQuery(id+"F5.boolean.opBoolean","SPLIT",FACE,{"disambiguationData":[TD([makeQuery(id+"F2.opExtrude","SWEPT_FACE",FACE,{"disambiguationData":[OSD([subQ5])]})])],"derivedFrom":makeQuery(id+"F3.boolean.opBoolean","COPY",FACE,{"derivedFrom":makeQuery(id+"F3.opExtrude","CAP_FACE",FACE,{"disambiguationData":[OSD([subQ5,subQ1,subQ6,subQ7,subQ4,subQ3,subQ2,subQ0])],"isStart":false})})}),makeQuery(id+"F8.opExtrude","SWEPT_FACE",FACE,{"disambiguationData":[OSD([sQuery(id+"F7.wireOp",EDGE,"E67")])]})]});}
            var Q5;
            Q5=makeQuery(id+"F8.boolean.opBoolean","INTERSECT",EDGE,{"disambiguationData":[OD(0.0)],"derivedFrom":[makeQuery(id+"F5.opExtrude","SWEPT_FACE",FACE,{"disambiguationData":[OSD([sQuery(id+"F4.wireOp",EDGE,"E30")])]}),makeQuery(id+"F8.opExtrude","SWEPT_FACE",FACE,{"disambiguationData":[OSD([sQuery(id+"F7.wireOp",EDGE,"E67")])]})]});
            fillet(context, id + "F14", {"entities" : qUnion([Q0, Q1, Q2, Q3, Q4, Q5]), "radius" : 3 * mm, "tangentPropagation" : true, "allowEdgeOverflow" : false});
        }
        {
            var Q0;
            Q0=makeQuery(id+"F1.opExtrude","CAP_EDGE",EDGE,{"disambiguationData":[OSD([sQuery(id+"F0.wireOp",EDGE,"E1.bottom")])],"isStart":false});
            fillet(context, id + "F15", {"entities" : qUnion([Q0]), "radius" : 2 * mm, "tangentPropagation" : true, "allowEdgeOverflow" : false});
        }
        {
            var Q0;
            {var subQ0=sQuery(id+"F0.wireOp",EDGE,"E1.bottom");var subQ1=sQuery(id+"F0.wireOp",EDGE,"E1.top");var subQ2=sQuery(id+"F0.wireOp",EDGE,"E1.left");var subQ3=sQuery(id+"F0.wireOp",EDGE,"E1.right");var subQ4=sQuery(id+"F0.wireOp",EDGE,"E4");var subQ5=sQuery(id+"F0.wireOp",EDGE,"E5");var subQ6=sQuery(id+"F0.wireOp",EDGE,"E6");var subQ7=sQuery(id+"F0.wireOp",EDGE,"E7");var subQ8=sQuery(id+"F0.wireOp",EDGE,"E21.filletArc");var subQ9=sQuery(id+"F0.wireOp",EDGE,"E22.filletArc");var subQ10=sQuery(id+"F0.wireOp",EDGE,"E23.filletArc");var subQ11=sQuery(id+"F0.wireOp",EDGE,"E24.filletArc");Q0=makeQuery(id+"F2.boolean.opBoolean","SPLIT",FACE,{"disambiguationData":[TD([makeQuery(id+"F1.opExtrude","SWEPT_FACE",FACE,{"disambiguationData":[OSD([subQ0])]})])],"derivedFrom":makeQuery(id+"F1.opExtrude","CAP_FACE",FACE,{"disambiguationData":[OSD([subQ0,subQ1,subQ2,subQ3,subQ4,subQ5,subQ6,subQ7,subQ8,subQ9,subQ10,subQ11])],"isStart":true})});}
            var sketch = newSketch(context, id + "F16", { "sketchPlane" : qUnion([Q0])});
            skLineSegment(sketch, "E79.0", {"start": v(14.05, 38.38) * mm, "end": v(14.05, 198.38) * mm});
            skArc(sketch, "E79.1", {"start": v(24.05, 208.38) * mm, "mid": v(16.98, 205.45) * mm, "end": v(14.05, 198.38) * mm});
            skLineSegment(sketch, "E79.2", {"start": v(24.05, 208.38) * mm, "end": v(164.05, 208.38) * mm});
            skArc(sketch, "E79.3", {"start": v(174.05, 198.38) * mm, "mid": v(171.12, 205.45) * mm, "end": v(164.05, 208.38) * mm});
            skLineSegment(sketch, "E79.4", {"start": v(174.05, 38.38) * mm, "end": v(174.05, 198.38) * mm});
            skArc(sketch, "E79.5", {"start": v(164.05, 28.38) * mm, "mid": v(171.12, 31.31) * mm, "end": v(174.05, 38.38) * mm});
            skLineSegment(sketch, "E79.6", {"start": v(24.05, 28.38) * mm, "end": v(164.05, 28.38) * mm});
            skArc(sketch, "E79.7", {"start": v(14.05, 38.38) * mm, "mid": v(16.98, 31.31) * mm, "end": v(24.05, 28.38) * mm});
            skCircle(sketch, "E79.9", {"center": v(34.05, 50.88) * mm, "radius": 4 * mm});
            skCircle(sketch, "E79.10", {"center": v(34.05, 185.88) * mm, "radius": 4 * mm});
            skCircle(sketch, "E79.11", {"center": v(154.05, 185.88) * mm, "radius": 4 * mm});
            skCircle(sketch, "E79.12", {"center": v(154.05, 50.88) * mm, "radius": 4 * mm});
            skArc(sketch, "E79.14", {"start": v(37.9, 70.2) * mm, "mid": v(94.05, 50.88) * mm, "end": v(150.2, 70.2) * mm});
            skArc(sketch, "E79.15", {"start": v(150.2, 70.2) * mm, "mid": v(153.04, 73.7) * mm, "end": v(154.05, 78.09) * mm});
            skLineSegment(sketch, "E79.16", {"start": v(154.05, 158.68) * mm, "end": v(154.05, 78.09) * mm});
            skArc(sketch, "E79.17", {"start": v(154.05, 158.68) * mm, "mid": v(153.04, 163.06) * mm, "end": v(150.2, 166.56) * mm});
            skArc(sketch, "E79.18", {"start": v(150.2, 166.56) * mm, "mid": v(94.05, 185.88) * mm, "end": v(37.9, 166.56) * mm});
            skArc(sketch, "E79.19", {"start": v(37.9, 166.56) * mm, "mid": v(35.06, 163.06) * mm, "end": v(34.05, 158.68) * mm});
            skLineSegment(sketch, "E79.20", {"start": v(34.05, 158.68) * mm, "end": v(34.05, 78.09) * mm});
            skArc(sketch, "E79.21", {"start": v(34.05, 78.09) * mm, "mid": v(35.06, 73.7) * mm, "end": v(37.9, 70.2) * mm});
            skCircle(sketch, "E80", {"center": v(94.05, 238.38) * mm, "radius": 6 * mm});
            skLineSegment(sketch, "E81", {"start": v(94.05, 238.38) * mm, "end": v(94.05, 208.38) * mm, "construction": true});
            skLineSegment(sketch, "E82", {"start": v(79.05, 226.38) * mm, "end": v(79.05, 238.38) * mm});
            skLineSegment(sketch, "E83", {"start": v(109.05, 238.38) * mm, "end": v(109.05, 226.38) * mm});
            skArc(sketch, "E84", {"start": v(109.05, 238.38) * mm, "mid": v(94.05, 253.38) * mm, "end": v(79.05, 238.38) * mm});
            skLineSegment(sketch, "E85", {"start": v(14.05, 118.38) * mm, "end": v(174.05, 118.38) * mm, "construction": true});
            skLineSegment(sketch, "E86", {"start": v(109.05, 226.38) * mm, "end": v(127.05, 208.38) * mm});
            skLineSegment(sketch, "E87", {"start": v(79.05, 226.38) * mm, "end": v(61.05, 208.38) * mm});
            skLineSegment(sketch, "E88.MirrorCS", {"start": v(79.05, 10.38) * mm, "end": v(61.05, 28.38) * mm});
            skLineSegment(sketch, "E89.MirrorCS", {"start": v(79.05, 10.38) * mm, "end": v(79.05, -1.62) * mm});
            skArc(sketch, "E90.MirrorCS", {"start": v(109.05, -1.62) * mm, "mid": v(94.05, -16.62) * mm, "end": v(79.05, -1.62) * mm});
            skLineSegment(sketch, "E91.MirrorCS", {"start": v(109.05, -1.62) * mm, "end": v(109.05, 10.38) * mm});
            skLineSegment(sketch, "E92.MirrorCS", {"start": v(109.05, 10.38) * mm, "end": v(127.05, 28.38) * mm});
            skLineSegment(sketch, "E93.MirrorCS", {"start": v(94.05, -1.62) * mm, "end": v(94.05, 28.38) * mm});
            skCircle(sketch, "E94.MirrorC", {"center": v(94.05, -1.62) * mm, "radius": 6 * mm});
            skSolve(sketch);
        }
        {
            var Q0;
            Q0 = qSketchRegion(id + "F16", true);
            var Q1;
            Q1=makeQuery(id+"F2.opExtrude","CAP_FACE",FACE,{"disambiguationData":[OSD([sQuery(id+"F0.wireOp",EDGE,"E12"),sQuery(id+"F0.wireOp",EDGE,"E13"),sQuery(id+"F0.wireOp",EDGE,"E14"),sQuery(id+"F0.wireOp",EDGE,"E15"),sQuery(id+"F0.wireOp",EDGE,"E17.filletArc"),sQuery(id+"F0.wireOp",EDGE,"E18.filletArc"),sQuery(id+"F0.wireOp",EDGE,"E19.filletArc"),sQuery(id+"F0.wireOp",EDGE,"E20.filletArc"),sQuery(id+"F0.wireOp",EDGE,"E25.0"),sQuery(id+"F0.wireOp",EDGE,"E25.1"),sQuery(id+"F0.wireOp",EDGE,"E25.2"),sQuery(id+"F0.wireOp",EDGE,"E25.3"),sQuery(id+"F0.wireOp",EDGE,"E25.4"),sQuery(id+"F0.wireOp",EDGE,"E25.5"),sQuery(id+"F0.wireOp",EDGE,"E25.6"),sQuery(id+"F0.wireOp",EDGE,"E25.7")])],"isStart":false});
            extrude(context, id + "F17", {"entities" : qUnion([Q0]), "operationType" : NewBodyOperationType.ADD, "endBound" : BoundingType.UP_TO_SURFACE, "endBoundEntityFace" : qUnion([Q1]), "depth" : 25 * mm});
        }
    });
